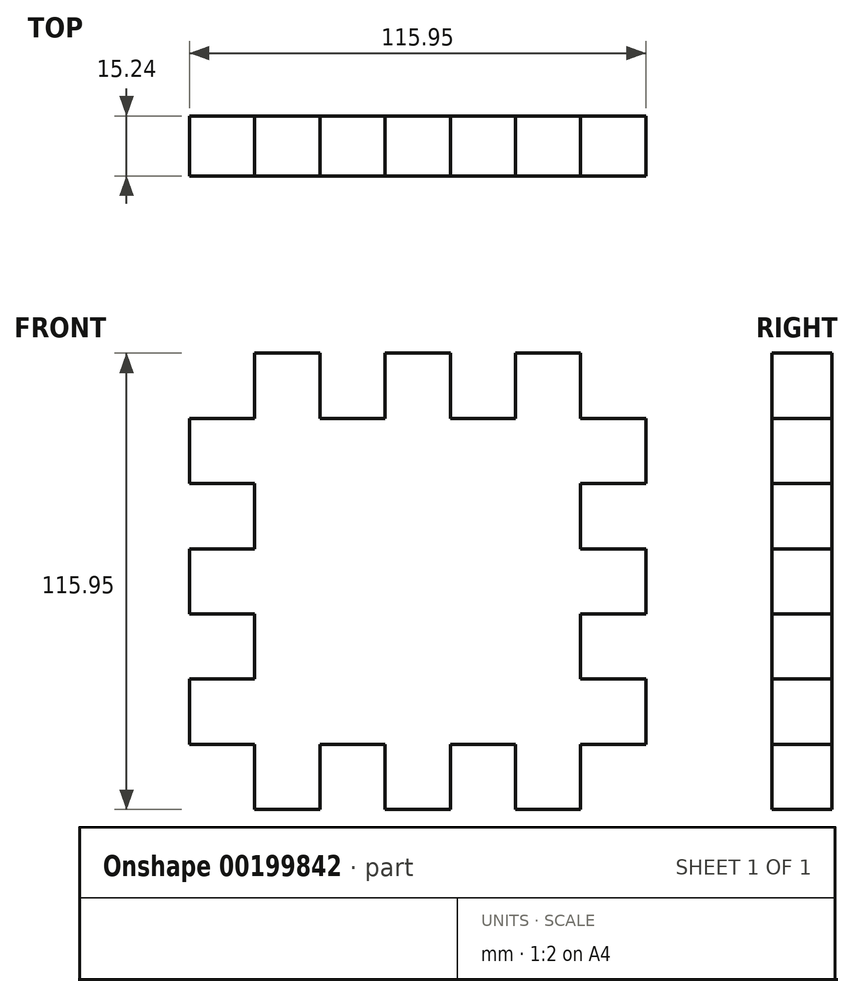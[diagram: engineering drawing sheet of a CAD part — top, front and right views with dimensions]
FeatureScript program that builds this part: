
annotation { "Feature Type Name" : "Feature", "Feature Type Description" : "" }
export const myFeature = defineFeature(function(context is Context, id is Id, definition is map)
    precondition{}
    {
        {
            var Q0;
            Q0=qCreatedBy(makeId("Front.planeOp"),FACE);
            var sketch = newSketch(context, id + "F0", { "sketchPlane" : qUnion([Q0])});
            skLineSegment(sketch, "E0", {"start": v(-58.62, 75.92) * mm, "end": v(-58.62, 59.35) * mm});
            skLineSegment(sketch, "E1", {"start": v(-58.62, 59.35) * mm, "end": v(-75.18, 59.35) * mm});
            skLineSegment(sketch, "E2", {"start": v(-75.18, 59.35) * mm, "end": v(-75.18, 42.79) * mm});
            skLineSegment(sketch, "E3", {"start": v(-75.18, 42.79) * mm, "end": v(-58.62, 42.79) * mm});
            skLineSegment(sketch, "E4", {"start": v(-58.62, 42.79) * mm, "end": v(-58.62, 26.22) * mm});
            skLineSegment(sketch, "E5", {"start": v(-58.62, 26.22) * mm, "end": v(-75.18, 26.22) * mm});
            skLineSegment(sketch, "E6", {"start": v(-75.18, 26.22) * mm, "end": v(-75.18, 9.66) * mm});
            skLineSegment(sketch, "E7", {"start": v(-75.18, 9.66) * mm, "end": v(-58.62, 9.66) * mm});
            skLineSegment(sketch, "E8", {"start": v(-58.62, 9.66) * mm, "end": v(-58.62, -6.9) * mm});
            skLineSegment(sketch, "E9", {"start": v(-58.62, -6.9) * mm, "end": v(-75.18, -6.9) * mm});
            skLineSegment(sketch, "E10", {"start": v(-75.18, -6.9) * mm, "end": v(-75.18, -23.47) * mm});
            skLineSegment(sketch, "E11", {"start": v(-75.18, -23.47) * mm, "end": v(-58.62, -23.47) * mm});
            skLineSegment(sketch, "E12", {"start": v(-58.62, -23.47) * mm, "end": v(-58.62, -40.03) * mm});
            skLineSegment(sketch, "E13", {"start": v(-58.62, -40.03) * mm, "end": v(-42.05, -40.03) * mm});
            skLineSegment(sketch, "E14", {"start": v(-42.05, -40.03) * mm, "end": v(-42.05, -23.47) * mm});
            skLineSegment(sketch, "E15", {"start": v(-42.05, -23.47) * mm, "end": v(-25.49, -23.47) * mm});
            skLineSegment(sketch, "E16", {"start": v(-25.49, -23.47) * mm, "end": v(-25.49, -40.03) * mm});
            skLineSegment(sketch, "E17", {"start": v(-25.49, -40.03) * mm, "end": v(-8.93, -40.03) * mm});
            skLineSegment(sketch, "E18", {"start": v(-8.93, -40.03) * mm, "end": v(-8.93, -23.47) * mm});
            skLineSegment(sketch, "E19", {"start": v(-8.93, -23.47) * mm, "end": v(7.64, -23.47) * mm});
            skLineSegment(sketch, "E20", {"start": v(7.64, -23.47) * mm, "end": v(7.64, -40.03) * mm});
            skLineSegment(sketch, "E21", {"start": v(7.64, -40.03) * mm, "end": v(24.2, -40.03) * mm});
            skLineSegment(sketch, "E22", {"start": v(24.2, -40.03) * mm, "end": v(24.2, -23.47) * mm});
            skLineSegment(sketch, "E23", {"start": v(24.2, -23.47) * mm, "end": v(40.77, -23.47) * mm});
            skLineSegment(sketch, "E24", {"start": v(40.77, -23.47) * mm, "end": v(40.77, -6.9) * mm});
            skLineSegment(sketch, "E25", {"start": v(40.77, -6.9) * mm, "end": v(24.2, -6.9) * mm});
            skLineSegment(sketch, "E26", {"start": v(24.2, -6.9) * mm, "end": v(24.2, 9.66) * mm});
            skLineSegment(sketch, "E27", {"start": v(24.2, 9.66) * mm, "end": v(40.77, 9.66) * mm});
            skLineSegment(sketch, "E28", {"start": v(40.77, 9.66) * mm, "end": v(40.77, 26.22) * mm});
            skLineSegment(sketch, "E29", {"start": v(40.77, 26.22) * mm, "end": v(24.2, 26.22) * mm});
            skLineSegment(sketch, "E30", {"start": v(24.2, 26.22) * mm, "end": v(24.2, 42.79) * mm});
            skLineSegment(sketch, "E31", {"start": v(24.2, 42.79) * mm, "end": v(40.77, 42.79) * mm});
            skLineSegment(sketch, "E32", {"start": v(40.77, 42.79) * mm, "end": v(40.77, 59.35) * mm});
            skLineSegment(sketch, "E33", {"start": v(40.77, 59.35) * mm, "end": v(24.2, 59.35) * mm});
            skLineSegment(sketch, "E34", {"start": v(24.2, 59.35) * mm, "end": v(24.2, 75.92) * mm});
            skLineSegment(sketch, "E35", {"start": v(24.2, 75.92) * mm, "end": v(7.64, 75.92) * mm});
            skLineSegment(sketch, "E36", {"start": v(7.64, 59.35) * mm, "end": v(-8.93, 59.35) * mm});
            skLineSegment(sketch, "E37", {"start": v(-8.93, 59.35) * mm, "end": v(-8.93, 75.92) * mm});
            skLineSegment(sketch, "E38", {"start": v(-8.93, 75.92) * mm, "end": v(-25.49, 75.92) * mm});
            skLineSegment(sketch, "E39", {"start": v(-25.49, 75.92) * mm, "end": v(-25.49, 59.35) * mm});
            skLineSegment(sketch, "E40", {"start": v(-25.49, 59.35) * mm, "end": v(-42.05, 59.35) * mm});
            skLineSegment(sketch, "E41", {"start": v(-42.05, 59.35) * mm, "end": v(-42.05, 75.92) * mm});
            skLineSegment(sketch, "E42", {"start": v(-42.05, 75.92) * mm, "end": v(-58.62, 75.92) * mm});
            skLineSegment(sketch, "E43", {"start": v(7.64, 75.92) * mm, "end": v(7.64, 59.35) * mm});
            skSolve(sketch);
        }
        {
            var Q0;
            Q0=makeQuery(id+"F0.imprint","IMPRINT",FACE,{"disambiguationData":[TD([[makeQuery(id+"F0.imprint","IMPRINT",EDGE,{"derivedFrom":sQuery(id+"F0.wireOp",EDGE,"E0")}),1.0]])]});
            extrude(context, id + "F1", {"entities" : qUnion([Q0]), "depth" : 15.24 * mm});
        }
    });
